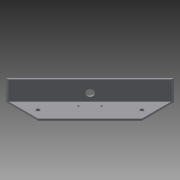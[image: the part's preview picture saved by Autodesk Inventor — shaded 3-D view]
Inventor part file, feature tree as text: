
AUTODESK INVENTOR PART (.ipt)
format: ipt  version: 2015 (Build 190159000, 159)  size: 127,488 bytes
history: native  units: in
note: dims shown in document units (in); Inventor stores cm internally (conversion verified against a paired STEP export)
features: extrude x3, sketch x2
ambient origin geometry x8: Origin, YZ Plane, XZ Plane, XY Plane, X Axis, Y Axis, Z Axis, Center Point
bodies: Solid1 (feature_tree)
feature tree (5):
  sketch  "Sketch1"  dims[d0=25.5906in d1=25.5906in]
  extrude  "Extrusion1"  Depth=25.5906in
  extrude  "Extrusion2"  Depth=0.1181in
  extrude  "Extrusion4"  Depth=0.3937in
  sketch  "Sketch2"  dims[d2=25.5906in d3=0.1181in d4=25.5906in d5=0.1181in d6=0.1181in d7=25.5906in d8=0.1181in d9=25.5906in d10=1.4567in d11=25.5906in d12=1.4567in d13=25.5906in d14=1.4567in d15=25.5906in d16=1.4567in d17=25.5906in d18=3.0709in d19=1.4567in d20=0.1181in d21=0.3937in d22=0.5709in d23=0.5709in d24=0.1181in d25=0.1181in d26=5.1181in d27=0.2362in d28=0.2362in d29=0.1181in d30=0.0in d31=1.4567in d32=0.0in d33=0.1181in d39=0.7874in d40=0.2756in d41=0.4724in d42=0.3937in d43=0.0in]
